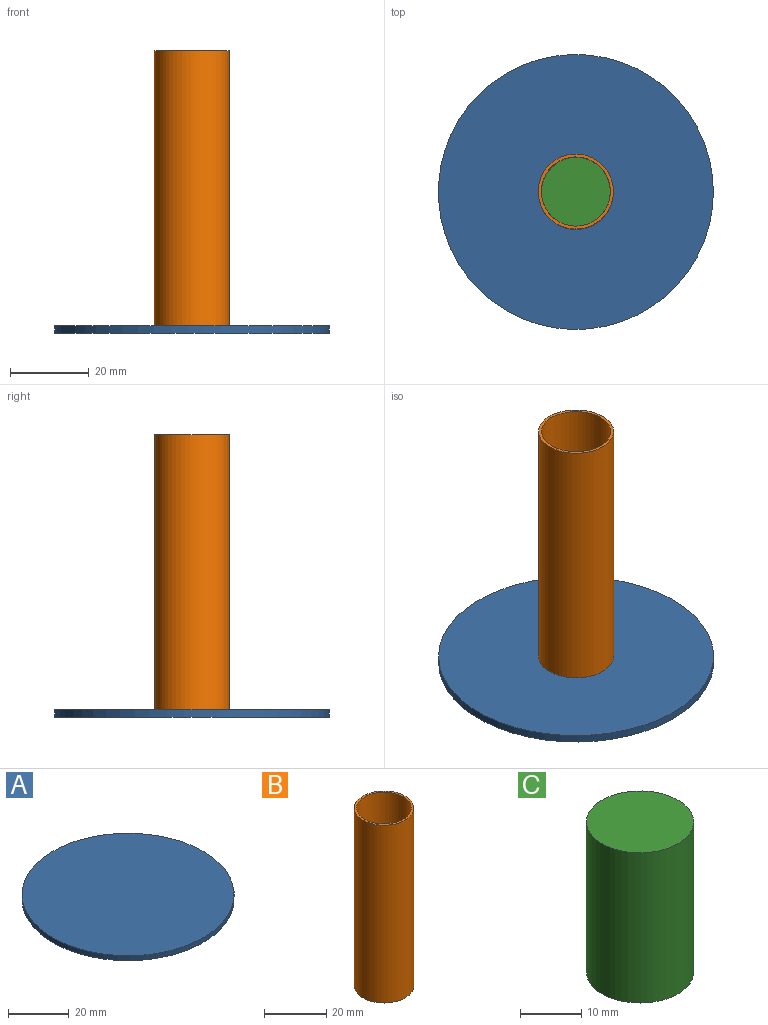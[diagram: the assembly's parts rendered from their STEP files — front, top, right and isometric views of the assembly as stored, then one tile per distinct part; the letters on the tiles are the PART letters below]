
ASSEMBLY  parts=3 mates=2
PART A: 3 faces, bbox 70x70x2 mm
  f0: cylinder r=35mm len=70mm, axis (0,0,-1), area 439.8mm2, adj f1,f2
  f1: plane 70x70mm, normal (0,0,1), area 3848.5mm2, adj f0
  f2: plane 70x70mm, normal (0,0,-1), area 3848.5mm2, adj f0
PART B: 4 faces, bbox 19.1x19.1x70 mm
  f0: cylinder r=8.8mm len=70mm, axis (0,0,-1), area 3870.4mm2, adj f2,f3
  f1: cylinder r=9.55mm len=70mm, axis (0,0,-1), area 4200.3mm2, adj f2,f3
  f2: plane 19.1x19.1mm, normal (0,0,1), area 43.2mm2, adj f0,f1
  f3: plane 19.1x19.1mm, normal (0,0,-1), area 43.2mm2, adj f0,f1
PART C: 3 faces, bbox 17.5x17.5x30 mm
  f0: cylinder r=8.75mm len=30mm, axis (0,0,-1), area 1649.3mm2, adj f1,f2
  f1: plane 17.5x17.5mm, normal (0,0,1), area 240.5mm2, adj f0
  f2: plane 17.5x17.5mm, normal (0,0,-1), area 240.5mm2, adj f0
PLACE A at identity
PLACE B t=(0,0,37)mm
PLACE C t=(0,0,24.37)mm
MATE fastened B.f0 <-> A.f0  axis (0,0,-1) through (0,0,2)mm
MATE slider C.f0 <-> B.f0  axis (0,0,1) through (0,0,39.37)mm
